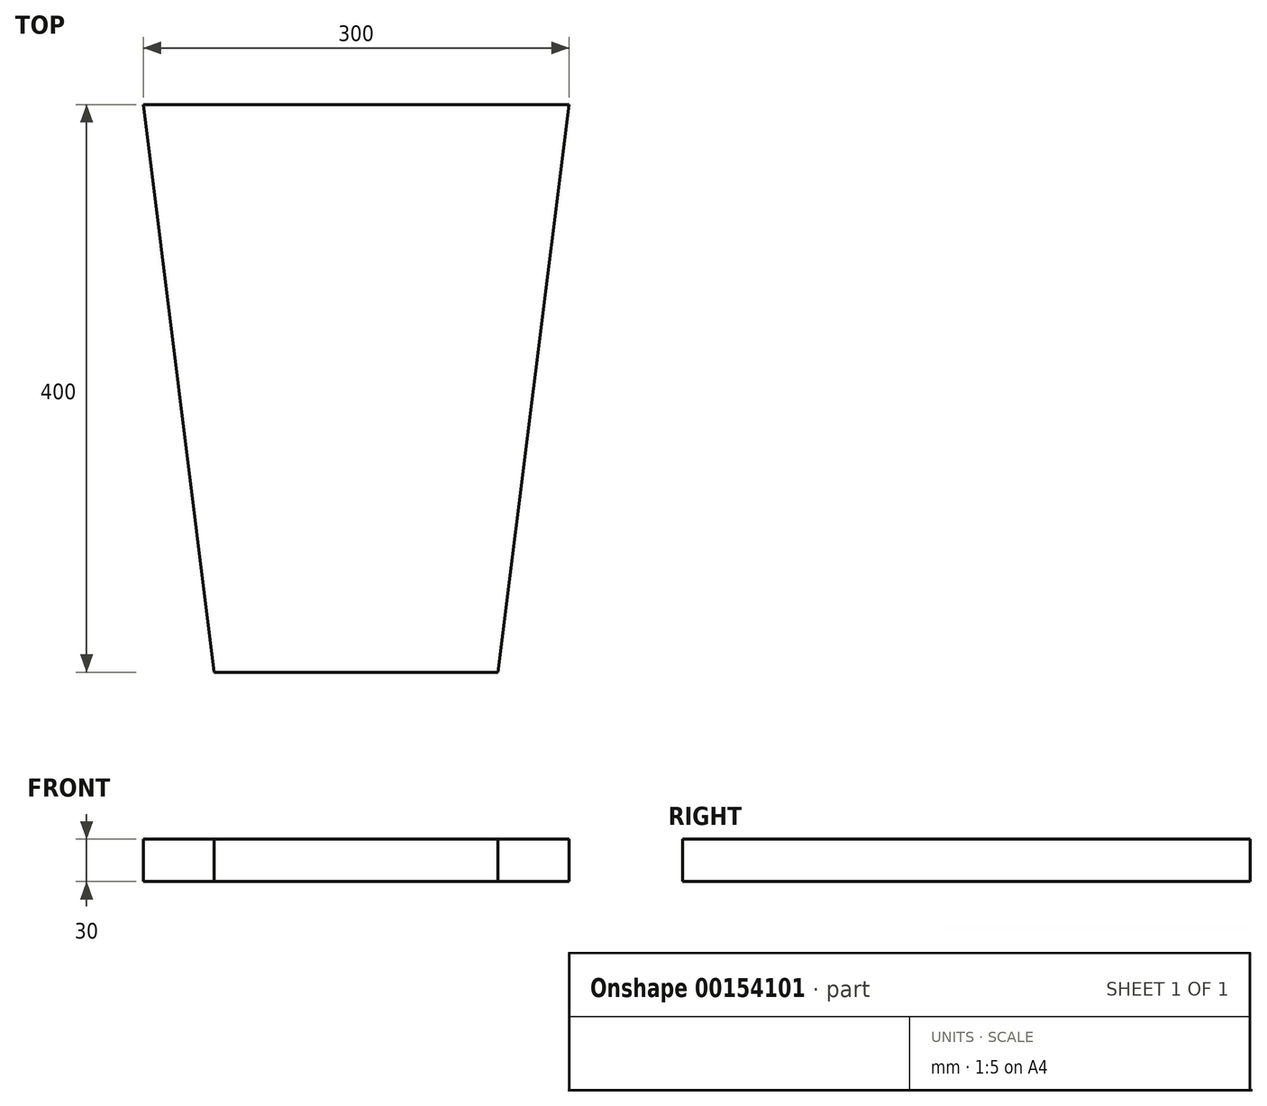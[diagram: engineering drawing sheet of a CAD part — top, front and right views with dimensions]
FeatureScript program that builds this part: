
annotation { "Feature Type Name" : "Feature", "Feature Type Description" : "" }
export const myFeature = defineFeature(function(context is Context, id is Id, definition is map)
    precondition{}
    {
        {
            var Q0;
            Q0=qCreatedBy(makeId("Top.planeOp"),FACE);
            var sketch = newSketch(context, id + "F0", { "sketchPlane" : qUnion([Q0])});
            skLineSegment(sketch, "E0", {"start": v(0, 203.21) * mm, "end": v(150, 203.21) * mm});
            skLineSegment(sketch, "E1", {"start": v(150, 203.21) * mm, "end": v(100, -196.79) * mm});
            skLineSegment(sketch, "E2", {"start": v(100, -196.79) * mm, "end": v(0, -196.79) * mm});
            skLineSegment(sketch, "E3.MirrorCS", {"start": v(0, 203.21) * mm, "end": v(-150, 203.21) * mm});
            skLineSegment(sketch, "E4.MirrorCS", {"start": v(-150, 203.21) * mm, "end": v(-100, -196.79) * mm});
            skLineSegment(sketch, "E5.MirrorCS", {"start": v(-100, -196.79) * mm, "end": v(0, -196.79) * mm});
            skSolve(sketch);
        }
        {
            var Q0;
            Q0=makeQuery(id+"F0.imprint","IMPRINT",FACE,{"disambiguationData":[TD([[makeQuery(id+"F0.imprint","IMPRINT",EDGE,{"derivedFrom":sQuery(id+"F0.wireOp",EDGE,"E0")}),-1.0]])]});
            extrude(context, id + "F1", {"entities" : qUnion([Q0]), "depth" : 30 * mm});
        }
    });
